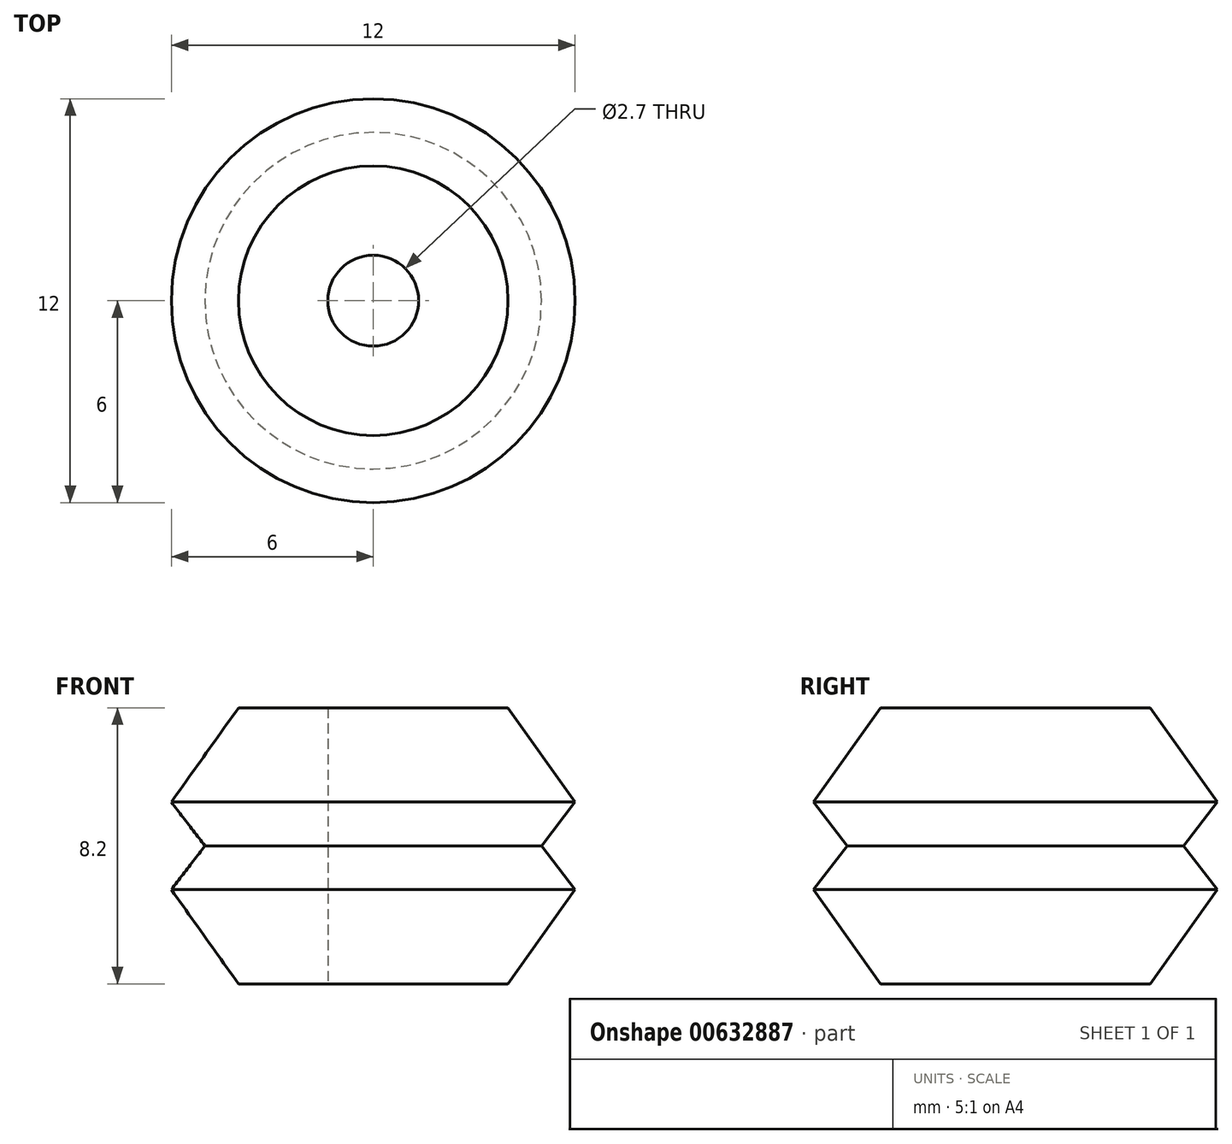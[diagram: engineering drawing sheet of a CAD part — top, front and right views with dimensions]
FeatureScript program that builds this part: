
annotation { "Feature Type Name" : "Feature", "Feature Type Description" : "" }
export const myFeature = defineFeature(function(context is Context, id is Id, definition is map)
    precondition{}
    {
        {
            var Q0;
            Q0=qCreatedBy(makeId("Front.planeOp"),FACE);
            var sketch = newSketch(context, id + "F0", { "sketchPlane" : qUnion([Q0])});
            skLineSegment(sketch, "E0", {"start": v(-1.35, 0) * mm, "end": v(-1.35, 4.1) * mm});
            skLineSegment(sketch, "E1", {"start": v(-1.35, 4.1) * mm, "end": v(-4, 4.1) * mm});
            skLineSegment(sketch, "E2", {"start": v(-4, 4.1) * mm, "end": v(-6, 1.3) * mm});
            skLineSegment(sketch, "E3", {"start": v(-6, 1.3) * mm, "end": v(-5, 0) * mm});
            skLineSegment(sketch, "E4.MirrorCS", {"start": v(-6, -1.3) * mm, "end": v(-5, 0) * mm});
            skLineSegment(sketch, "E5.MirrorCS", {"start": v(-4, -4.1) * mm, "end": v(-6, -1.3) * mm});
            skLineSegment(sketch, "E6.MirrorCS", {"start": v(-1.35, -4.1) * mm, "end": v(-4, -4.1) * mm});
            skLineSegment(sketch, "E7.MirrorCS", {"start": v(-1.35, 0) * mm, "end": v(-1.35, -4.1) * mm});
            skLineSegment(sketch, "E8", {"start": v(0, 0) * mm, "end": v(0, 1.83) * mm});
            skSolve(sketch);
        }
        {
            var Q0;
            Q0=makeQuery(id+"F0.imprint","IMPRINT",FACE,{"disambiguationData":[TD([[makeQuery(id+"F0.imprint","IMPRINT",EDGE,{"derivedFrom":sQuery(id+"F0.wireOp",EDGE,"E0")}),1.0]])]});
            var Q1;
            Q1=sQuery(id+"F0.wireOp",EDGE,"E8");
            revolve(context, id + "F1", {"entities" : qUnion([Q0]), "axis" : qUnion([Q1]), "revolveType" : RevolveType.FULL});
        }
    });
